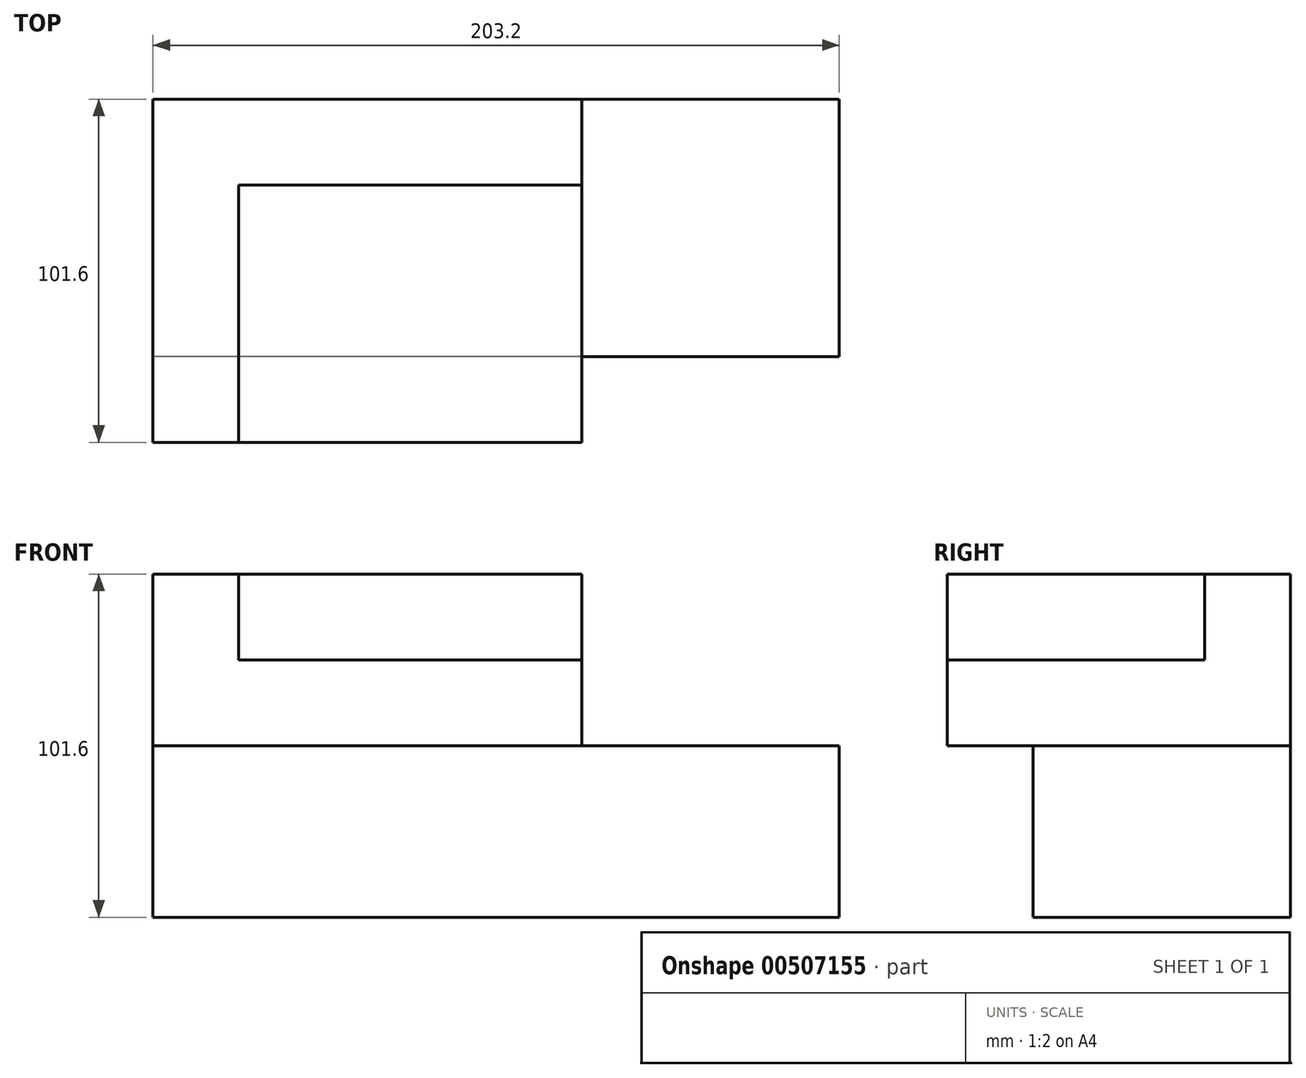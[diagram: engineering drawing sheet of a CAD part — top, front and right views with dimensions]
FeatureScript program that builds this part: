
annotation { "Feature Type Name" : "Feature", "Feature Type Description" : "" }
export const myFeature = defineFeature(function(context is Context, id is Id, definition is map)
    precondition{}
    {
        {
            var Q0;
            Q0=qCreatedBy(makeId("Top.planeOp"),FACE);
            var sketch = newSketch(context, id + "F0", { "sketchPlane" : qUnion([Q0])});
            skLineSegment(sketch, "E0", {"start": v(-64.5, 63.31) * mm, "end": v(-64.5, -38.29) * mm});
            skLineSegment(sketch, "E1", {"start": v(-64.5, -38.29) * mm, "end": v(62.5, -38.29) * mm});
            skLineSegment(sketch, "E2", {"start": v(62.5, -38.29) * mm, "end": v(62.5, 63.31) * mm});
            skLineSegment(sketch, "E3", {"start": v(62.5, 63.31) * mm, "end": v(-64.5, 63.31) * mm});
            skSolve(sketch);
        }
        {
            var Q0;
            Q0 = qSketchRegion(id + "F0", true);
            extrude(context, id + "F1", {"entities" : qUnion([Q0]), "depth" : 50.8 * mm});
        }
        {
            var Q0;
            Q0=makeQuery(id+"F1.opExtrude","CAP_FACE",FACE,{"disambiguationData":[OSD([sQuery(id+"F0.wireOp",EDGE,"E0"),sQuery(id+"F0.wireOp",EDGE,"E1"),sQuery(id+"F0.wireOp",EDGE,"E2"),sQuery(id+"F0.wireOp",EDGE,"E3")])],"isStart":false});
            var sketch = newSketch(context, id + "F2", { "sketchPlane" : qUnion([Q0])});
            skLineSegment(sketch, "E4", {"start": v(62.5, 37.91) * mm, "end": v(-39.1, 37.91) * mm});
            skLineSegment(sketch, "E5", {"start": v(-39.1, 37.91) * mm, "end": v(-39.1, -38.29) * mm});
            skLineSegment(sketch, "E6", {"start": v(-39.1, -38.29) * mm, "end": v(62.5, -38.29) * mm});
            skLineSegment(sketch, "E7", {"start": v(62.5, -38.29) * mm, "end": v(62.5, 37.91) * mm});
            skSolve(sketch);
        }
        {
            var Q0;
            Q0 = qSketchRegion(id + "F2", true);
            extrude(context, id + "F3", {"entities" : qUnion([Q0]), "operationType" : NewBodyOperationType.REMOVE, "oppositeDirection" : true, "depth" : 25.4 * mm});
        }
        {
            var Q0;
            Q0=makeQuery(id+"F1.opExtrude","CAP_FACE",FACE,{"disambiguationData":[OSD([sQuery(id+"F0.wireOp",EDGE,"E0"),sQuery(id+"F0.wireOp",EDGE,"E1"),sQuery(id+"F0.wireOp",EDGE,"E2"),sQuery(id+"F0.wireOp",EDGE,"E3")])],"isStart":true});
            var sketch = newSketch(context, id + "F4", { "sketchPlane" : qUnion([Q0])});
            skLineSegment(sketch, "E8", {"start": v(-64.5, -63.31) * mm, "end": v(138.7, -63.31) * mm});
            skLineSegment(sketch, "E9", {"start": v(138.7, -63.31) * mm, "end": v(138.7, 12.89) * mm});
            skLineSegment(sketch, "E10", {"start": v(138.7, 12.89) * mm, "end": v(-64.5, 12.89) * mm});
            skLineSegment(sketch, "E11", {"start": v(-64.5, 12.89) * mm, "end": v(-64.5, -63.31) * mm});
            skSolve(sketch);
        }
        {
            var Q0;
            Q0 = qSketchRegion(id + "F4", true);
            extrude(context, id + "F5", {"entities" : qUnion([Q0]), "operationType" : NewBodyOperationType.ADD, "depth" : 50.8 * mm});
        }
    });
